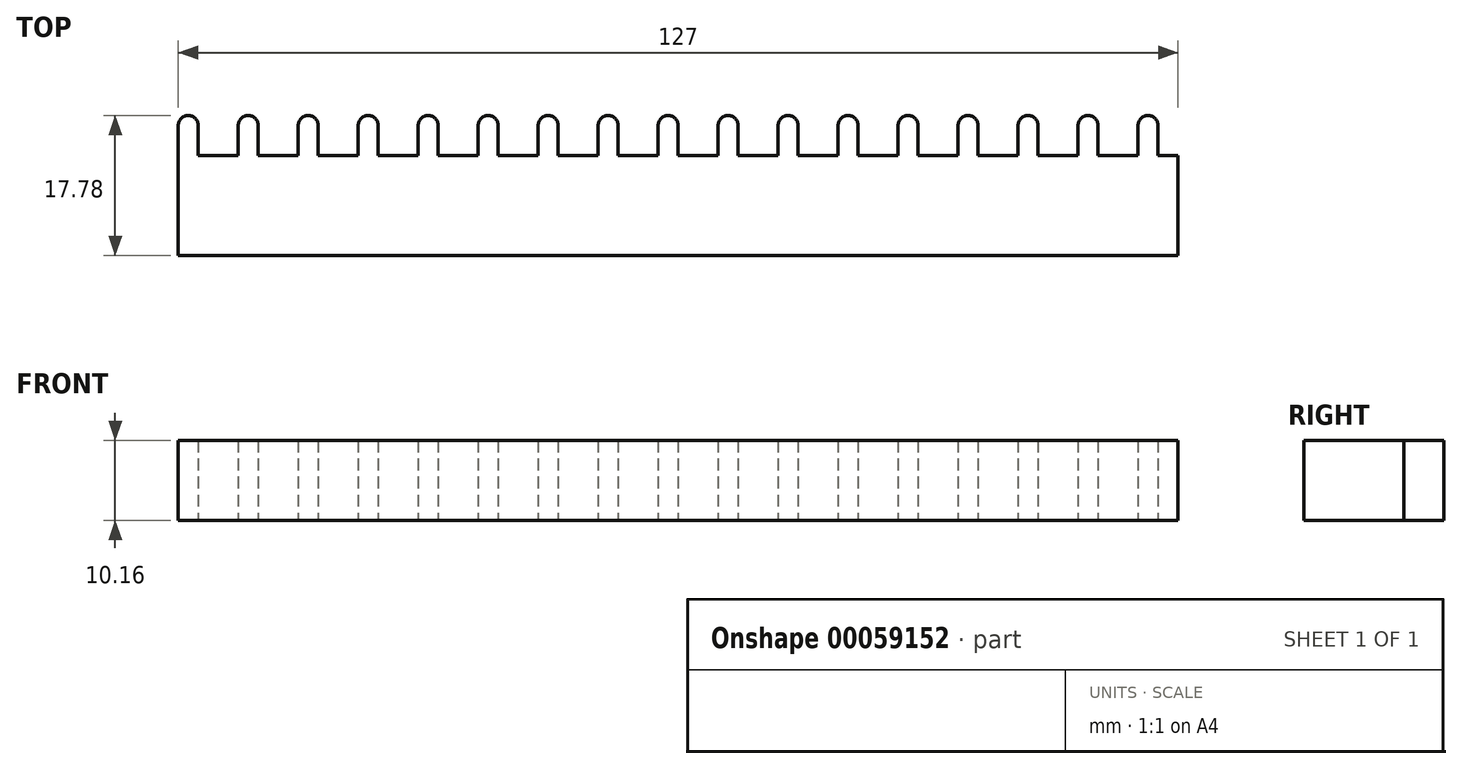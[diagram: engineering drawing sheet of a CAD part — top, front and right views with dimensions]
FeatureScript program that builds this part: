
annotation { "Feature Type Name" : "Feature", "Feature Type Description" : "" }
export const myFeature = defineFeature(function(context is Context, id is Id, definition is map)
    precondition{}
    {
        {
            var Q0;
            Q0=qCreatedBy(makeId("Top.planeOp"),FACE);
            var sketch = newSketch(context, id + "F0", { "sketchPlane" : qUnion([Q0])});
            skLineSegment(sketch, "E0", {"start": v(-63.5, -6.35) * mm, "end": v(-63.5, 6.35) * mm});
            skLineSegment(sketch, "E1", {"start": v(-63.5, 6.35) * mm, "end": v(-63.5, 10.16) * mm});
            skLineSegment(sketch, "E2", {"start": v(-60.96, 10.16) * mm, "end": v(-60.96, 6.35) * mm});
            skArc(sketch, "E3", {"start": v(-60.96, 10.16) * mm, "mid": v(-62.23, 11.43) * mm, "end": v(-63.5, 10.16) * mm});
            skLineSegment(sketch, "E4", {"start": v(-63.5, -6.35) * mm, "end": v(63.5, -6.35) * mm});
            skLineSegment(sketch, "E5", {"start": v(63.5, -6.35) * mm, "end": v(63.5, 6.35) * mm});
            skLineSegment(sketch, "E6", {"start": v(63.5, 6.35) * mm, "end": v(-60.96, 6.35) * mm});
            skLineSegment(sketch, "E7.1.0.0", {"start": v(-55.88, 6.35) * mm, "end": v(-55.88, 10.16) * mm});
            skArc(sketch, "E7.1.0.1", {"start": v(-53.34, 10.16) * mm, "mid": v(-54.61, 11.43) * mm, "end": v(-55.88, 10.16) * mm});
            skLineSegment(sketch, "E7.1.0.2", {"start": v(-53.34, 10.16) * mm, "end": v(-53.34, 6.35) * mm});
            skLineSegment(sketch, "E7.2.0.0", {"start": v(-48.26, 6.35) * mm, "end": v(-48.26, 10.16) * mm});
            skArc(sketch, "E7.2.0.1", {"start": v(-45.72, 10.16) * mm, "mid": v(-47, 11.43) * mm, "end": v(-48.26, 10.16) * mm});
            skLineSegment(sketch, "E7.2.0.2", {"start": v(-45.72, 10.16) * mm, "end": v(-45.72, 6.35) * mm});
            skLineSegment(sketch, "E7.3.0.0", {"start": v(-40.64, 6.35) * mm, "end": v(-40.64, 10.16) * mm});
            skArc(sketch, "E7.3.0.1", {"start": v(-38.1, 10.16) * mm, "mid": v(-39.37, 11.43) * mm, "end": v(-40.64, 10.16) * mm});
            skLineSegment(sketch, "E7.3.0.2", {"start": v(-38.1, 10.16) * mm, "end": v(-38.1, 6.35) * mm});
            skLineSegment(sketch, "E7.4.0.0", {"start": v(-33.02, 6.35) * mm, "end": v(-33.02, 10.16) * mm});
            skArc(sketch, "E7.4.0.1", {"start": v(-30.48, 10.16) * mm, "mid": v(-31.75, 11.43) * mm, "end": v(-33.02, 10.16) * mm});
            skLineSegment(sketch, "E7.4.0.2", {"start": v(-30.48, 10.16) * mm, "end": v(-30.48, 6.35) * mm});
            skLineSegment(sketch, "E7.5.0.0", {"start": v(-25.4, 6.35) * mm, "end": v(-25.4, 10.16) * mm});
            skArc(sketch, "E7.5.0.1", {"start": v(-22.86, 10.16) * mm, "mid": v(-24.13, 11.43) * mm, "end": v(-25.4, 10.16) * mm});
            skLineSegment(sketch, "E7.5.0.2", {"start": v(-22.86, 10.16) * mm, "end": v(-22.86, 6.35) * mm});
            skLineSegment(sketch, "E7.6.0.0", {"start": v(-17.78, 6.35) * mm, "end": v(-17.78, 10.16) * mm});
            skArc(sketch, "E7.6.0.1", {"start": v(-15.24, 10.16) * mm, "mid": v(-16.51, 11.43) * mm, "end": v(-17.78, 10.16) * mm});
            skLineSegment(sketch, "E7.6.0.2", {"start": v(-15.24, 10.16) * mm, "end": v(-15.24, 6.35) * mm});
            skLineSegment(sketch, "E7.7.0.0", {"start": v(-10.16, 6.35) * mm, "end": v(-10.16, 10.16) * mm});
            skArc(sketch, "E7.7.0.1", {"start": v(-7.62, 10.16) * mm, "mid": v(-8.9, 11.43) * mm, "end": v(-10.16, 10.16) * mm});
            skLineSegment(sketch, "E7.7.0.2", {"start": v(-7.62, 10.16) * mm, "end": v(-7.62, 6.35) * mm});
            skLineSegment(sketch, "E7.8.0.0", {"start": v(-2.54, 6.35) * mm, "end": v(-2.54, 10.16) * mm});
            skArc(sketch, "E7.8.0.1", {"start": v(0, 10.16) * mm, "mid": v(-1.27, 11.43) * mm, "end": v(-2.54, 10.16) * mm});
            skLineSegment(sketch, "E7.8.0.2", {"start": v(0, 10.16) * mm, "end": v(0, 6.35) * mm});
            skLineSegment(sketch, "E7.9.0.0", {"start": v(5.08, 6.35) * mm, "end": v(5.08, 10.16) * mm});
            skArc(sketch, "E7.9.0.1", {"start": v(7.62, 10.16) * mm, "mid": v(6.35, 11.43) * mm, "end": v(5.08, 10.16) * mm});
            skLineSegment(sketch, "E7.9.0.2", {"start": v(7.62, 10.16) * mm, "end": v(7.62, 6.35) * mm});
            skLineSegment(sketch, "E7.10.0.0", {"start": v(12.7, 6.35) * mm, "end": v(12.7, 10.16) * mm});
            skArc(sketch, "E7.10.0.1", {"start": v(15.24, 10.16) * mm, "mid": v(13.97, 11.43) * mm, "end": v(12.7, 10.16) * mm});
            skLineSegment(sketch, "E7.10.0.2", {"start": v(15.24, 10.16) * mm, "end": v(15.24, 6.35) * mm});
            skLineSegment(sketch, "E7.11.0.0", {"start": v(20.32, 6.35) * mm, "end": v(20.32, 10.16) * mm});
            skArc(sketch, "E7.11.0.1", {"start": v(22.86, 10.16) * mm, "mid": v(21.6, 11.43) * mm, "end": v(20.32, 10.16) * mm});
            skLineSegment(sketch, "E7.11.0.2", {"start": v(22.86, 10.16) * mm, "end": v(22.86, 6.35) * mm});
            skLineSegment(sketch, "E7.12.0.0", {"start": v(27.94, 6.35) * mm, "end": v(27.94, 10.16) * mm});
            skArc(sketch, "E7.12.0.1", {"start": v(30.48, 10.16) * mm, "mid": v(29.21, 11.43) * mm, "end": v(27.94, 10.16) * mm});
            skLineSegment(sketch, "E7.12.0.2", {"start": v(30.48, 10.16) * mm, "end": v(30.48, 6.35) * mm});
            skLineSegment(sketch, "E7.13.0.0", {"start": v(35.56, 6.35) * mm, "end": v(35.56, 10.16) * mm});
            skArc(sketch, "E7.13.0.1", {"start": v(38.1, 10.16) * mm, "mid": v(36.83, 11.43) * mm, "end": v(35.56, 10.16) * mm});
            skLineSegment(sketch, "E7.13.0.2", {"start": v(38.1, 10.16) * mm, "end": v(38.1, 6.35) * mm});
            skLineSegment(sketch, "E7.14.0.0", {"start": v(43.18, 6.35) * mm, "end": v(43.18, 10.16) * mm});
            skArc(sketch, "E7.14.0.1", {"start": v(45.72, 10.16) * mm, "mid": v(44.45, 11.43) * mm, "end": v(43.18, 10.16) * mm});
            skLineSegment(sketch, "E7.14.0.2", {"start": v(45.72, 10.16) * mm, "end": v(45.72, 6.35) * mm});
            skLineSegment(sketch, "E7.15.0.0", {"start": v(50.8, 6.35) * mm, "end": v(50.8, 10.16) * mm});
            skArc(sketch, "E7.15.0.1", {"start": v(53.34, 10.16) * mm, "mid": v(52.07, 11.43) * mm, "end": v(50.8, 10.16) * mm});
            skLineSegment(sketch, "E7.15.0.2", {"start": v(53.34, 10.16) * mm, "end": v(53.34, 6.35) * mm});
            skLineSegment(sketch, "E7.16.0.0", {"start": v(58.42, 6.35) * mm, "end": v(58.42, 10.16) * mm});
            skArc(sketch, "E7.16.0.1", {"start": v(60.96, 10.16) * mm, "mid": v(59.7, 11.43) * mm, "end": v(58.42, 10.16) * mm});
            skLineSegment(sketch, "E7.16.0.2", {"start": v(60.96, 10.16) * mm, "end": v(60.96, 6.35) * mm});
            skLineSegment(sketch, "E7.direction1", {"start": v(-63.5, 6.35) * mm, "end": v(-55.88, 6.35) * mm, "construction": true});
            skSolve(sketch);
        }
        {
            var Q0;
            Q0 = qSketchRegion(id + "F0", true);
            extrude(context, id + "F1", {"entities" : qUnion([Q0]), "depth" : 10.16 * mm});
        }
    });
